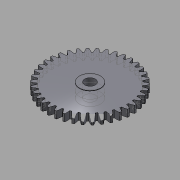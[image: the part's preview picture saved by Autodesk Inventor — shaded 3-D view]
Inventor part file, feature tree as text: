
AUTODESK INVENTOR PART (.ipt)
format: ipt  version: 2015 (Build 190159000, 159)  size: 333,824 bytes
history: native  units: in
note: dims shown in document units (in); Inventor stores cm internally (conversion verified against a paired STEP export)
features: other x13, sketch x5, plane x2
ambient origin geometry x8: Origin, YZ Plane, XZ Plane, XY Plane, X Axis, Y Axis, Z Axis, Center Point
bodies: Solid1 (feature_tree)
feature tree (20):
  other  "Spur Gear2"
  other  "Solid1::Spur Gear2"
  other  "TaggingFeature1"
  sketch  "Sketch1"  dims[d0=0.3937in]
  sketch  "Sketch2"  dims[d16=0.5709in d17=0.0in d41=0.0in d43=0.5709in d46=0.5709in d47=0.0in d48=0.0in]
  sketch  "Sketch3"
  sketch  "Sketch4"
  sketch  "Sketch5"
  plane  "XZ Plane_1"
  plane  "Work Plane2"
  other  "Z Axis_1"
  other  "Srf1"
  other  "Srf1::Derived"
  other  "Distance iMate"
  other  "Align iMate"
  other  "Mesh iMate"
  other  "Axis iMate"
  other  "Position iMate"
  other  "Mesh iMate2"
  other  "Start plane iMate"
